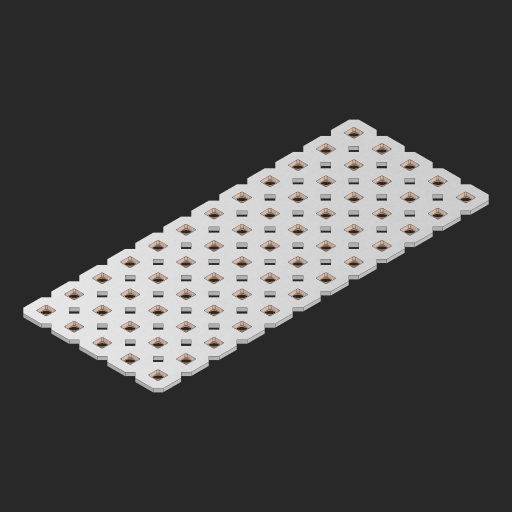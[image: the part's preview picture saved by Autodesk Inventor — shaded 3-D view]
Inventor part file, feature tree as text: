
AUTODESK INVENTOR PART (.ipt)
format: ipt  version: 2023 (Build 270158000, 158)  size: 985,600 bytes
history: native  units: in
note: dims shown in document units (in); Inventor stores cm internally (conversion verified against a paired STEP export)
features: other x61, extrude x59, sketch x2, pattern_linear x1
ambient origin geometry x8: Origin, YZ Plane, XZ Plane, XY Plane, X Axis, Y Axis, Z Axis, Center Point
bodies: Solid1 (feature_tree), Body (feature_tree)
feature tree (123):
  pattern_linear  "Rectangular Pattern1"  Spacing1=0.09in  [1 undecoded]
  sketch  "Sketch1"  dims[d1=0.5in]
  sketch  "Sketch2"  dims[d2=0.182in d3=0.09in d4=0.09in d5=0.09in d6=0.09in d7=0.09in d8=0.09in d9=0.09in d10=0.09in d11=0.02in d13=0.0in d14=0.172in d15=0.0625in d16=0.0in d19=0.5in d22=0.5in]
  other  "Srf1"
  other  "Srf126"
  other  "Srf127"
  other  "Srf128"
  other  "Srf129"
  other  "Srf130"
  other  "Srf131"
  other  "Srf250"
  other  "Srf251"
  other  "Srf252"
  other  "Srf253"
  other  "Srf254"
  other  "Srf268"
  other  "Srf269"
  other  "Srf270"
  other  "Srf271"
  other  "Srf272"
  other  "Srf273"
  other  "Srf274"
  other  "Srf275"
  other  "Srf276"
  other  "Srf277"
  other  "Srf278"
  other  "Srf279"
  other  "Srf293"
  other  "Srf294"
  other  "Srf295"
  other  "Srf296"
  other  "Srf297"
  other  "Srf298"
  other  "Srf299"
  other  "Srf300"
  other  "Srf301"
  other  "Srf302"
  other  "Srf303"
  other  "Srf304"
  other  "Srf318"
  other  "Srf319"
  other  "Srf320"
  other  "Srf321"
  other  "Srf322"
  other  "Srf323"
  other  "Srf324"
  other  "Srf325"
  other  "Srf326"
  other  "Srf327"
  other  "Srf328"
  other  "Srf329"
  other  "Srf343"
  other  "Srf344"
  other  "Srf345"
  other  "Srf346"
  other  "Srf347"
  other  "Srf348"
  other  "Srf349"
  other  "Srf350"
  other  "Srf351"
  other  "Srf352"
  other  "Srf353"
  other  "Srf354"
  other  "Circle"
  extrude  "ExtrusionSrf126"  Depth=0.09in
  extrude  "ExtrusionSrf127"  Depth=0.09in
  extrude  "ExtrusionSrf128"  Depth=0.09in
  extrude  "ExtrusionSrf129"  Depth=0.09in
  extrude  "ExtrusionSrf130"  Depth=0.09in
  extrude  "ExtrusionSrf131"  Depth=0.09in
  extrude  "ExtrusionSrf250"  Depth=0.09in
  extrude  "ExtrusionSrf251"  Depth=0.02in
  extrude  "ExtrusionSrf252"  TaperAngle=0.0deg  [1 undecoded]
  extrude  "ExtrusionSrf253"  Depth=0.5in
  extrude  "ExtrusionSrf254"  Depth=0.0625in TaperAngle=0.0deg
  extrude  "ExtrusionSrf268"  Depth=0.5in
  extrude  "ExtrusionSrf269"  Depth=0.5in
  extrude  "ExtrusionSrf270"  [1 undecoded]
  extrude  "ExtrusionSrf271"  [1 undecoded]
  extrude  "ExtrusionSrf272"  [1 undecoded]
  extrude  "ExtrusionSrf273"  [1 undecoded]
  extrude  "ExtrusionSrf274"  [1 undecoded]
  extrude  "ExtrusionSrf275"  [1 undecoded]
  extrude  "ExtrusionSrf276"  [1 undecoded]
  extrude  "ExtrusionSrf277"  [1 undecoded]
  extrude  "ExtrusionSrf278"  [1 undecoded]
  extrude  "ExtrusionSrf279"  [1 undecoded]
  extrude  "ExtrusionSrf293"  [1 undecoded]
  extrude  "ExtrusionSrf294"  [1 undecoded]
  extrude  "ExtrusionSrf295"  [1 undecoded]
  extrude  "ExtrusionSrf296"  [1 undecoded]
  extrude  "ExtrusionSrf297"  [1 undecoded]
  extrude  "ExtrusionSrf298"  [1 undecoded]
  extrude  "ExtrusionSrf299"  [1 undecoded]
  extrude  "ExtrusionSrf300"  [1 undecoded]
  extrude  "ExtrusionSrf301"  [1 undecoded]
  extrude  "ExtrusionSrf302"  [1 undecoded]
  extrude  "ExtrusionSrf303"  [1 undecoded]
  extrude  "ExtrusionSrf304"  [1 undecoded]
  extrude  "ExtrusionSrf318"  [1 undecoded]
  extrude  "ExtrusionSrf319"  [1 undecoded]
  extrude  "ExtrusionSrf320"  [1 undecoded]
  extrude  "ExtrusionSrf321"  [1 undecoded]
  extrude  "ExtrusionSrf322"  [1 undecoded]
  extrude  "ExtrusionSrf323"  [1 undecoded]
  extrude  "ExtrusionSrf324"  [1 undecoded]
  extrude  "ExtrusionSrf325"  [1 undecoded]
  extrude  "ExtrusionSrf326"  [1 undecoded]
  extrude  "ExtrusionSrf327"  [1 undecoded]
  extrude  "ExtrusionSrf328"  [1 undecoded]
  extrude  "ExtrusionSrf329"  [1 undecoded]
  extrude  "ExtrusionSrf343"  [1 undecoded]
  extrude  "ExtrusionSrf344"  [1 undecoded]
  extrude  "ExtrusionSrf345"  [1 undecoded]
  extrude  "ExtrusionSrf346"  [1 undecoded]
  extrude  "ExtrusionSrf347"  [1 undecoded]
  extrude  "ExtrusionSrf348"  [1 undecoded]
  extrude  "ExtrusionSrf349"  [1 undecoded]
  extrude  "ExtrusionSrf350"  [1 undecoded]
  extrude  "ExtrusionSrf351"  [1 undecoded]
  extrude  "ExtrusionSrf352"  [1 undecoded]
  extrude  "ExtrusionSrf353"  [1 undecoded]
  extrude  "ExtrusionSrf354"  [1 undecoded]
note: 48 required parameter values undecoded (feature->parameter linkage not recoverable at this tier; creation-order binding heuristic only, values carry confidence <= 0.55)
